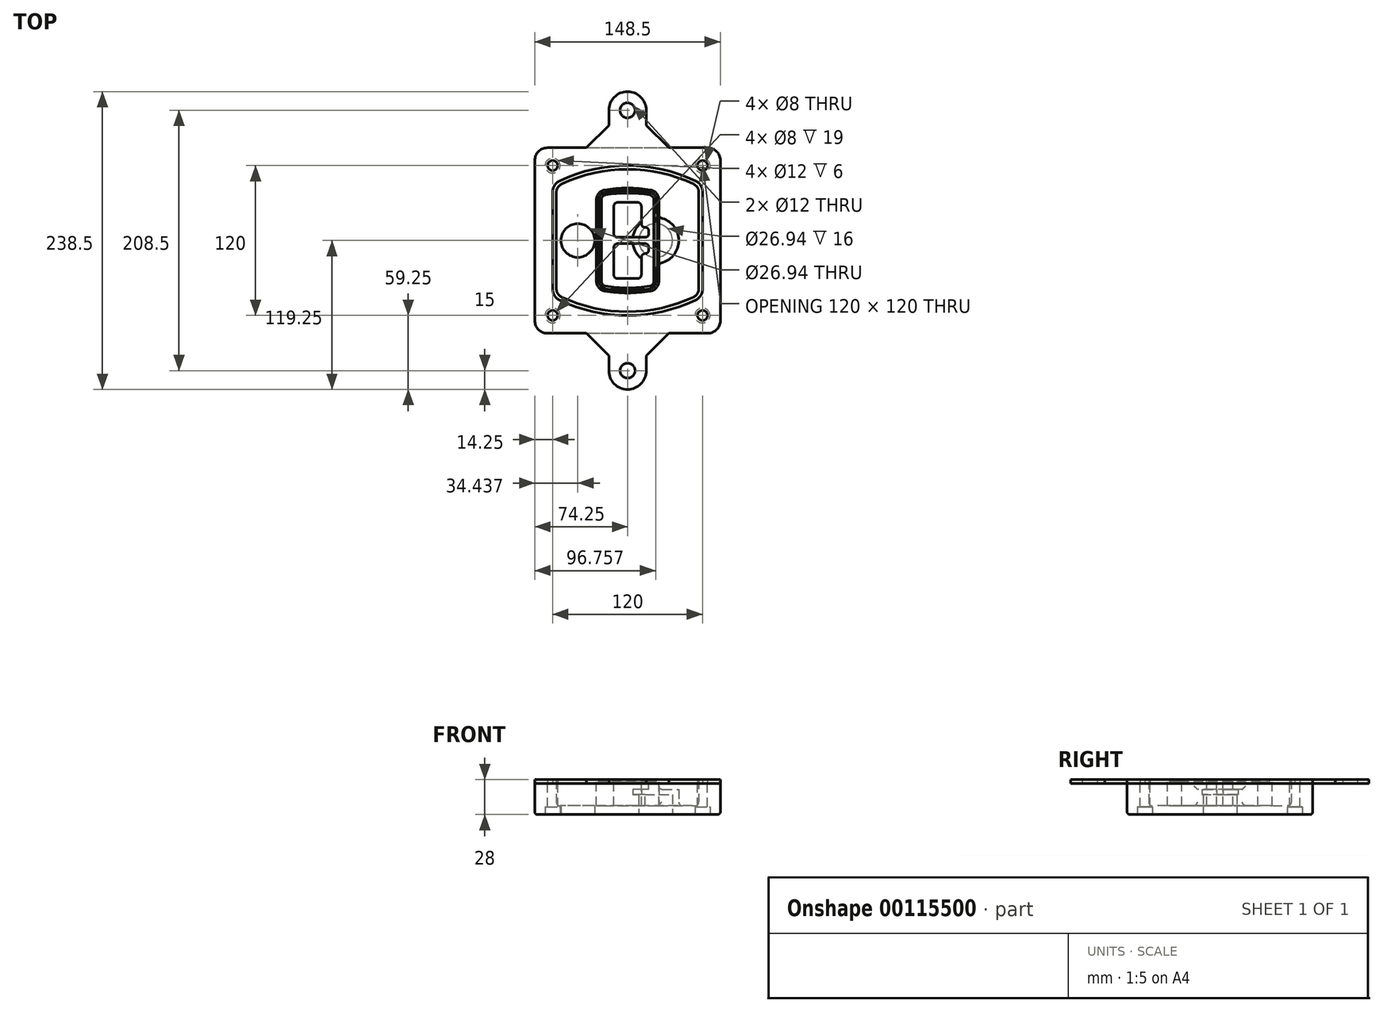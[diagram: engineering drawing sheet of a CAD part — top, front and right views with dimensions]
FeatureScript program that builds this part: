
annotation { "Feature Type Name" : "Feature", "Feature Type Description" : "" }
export const myFeature = defineFeature(function(context is Context, id is Id, definition is map)
    precondition{}
    {
        {
            var Q0;
            Q0=qCreatedBy(makeId("Top.planeOp"),FACE);
            var sketch = newSketch(context, id + "F0", { "sketchPlane" : qUnion([Q0])});
            skPoint(sketch, "E0.rect.middle", {"position": v(0, 0) * mm});
            skLineSegment(sketch, "E1.bottom", {"start": v(-64.25, -74.25) * mm, "end": v(64.25, -74.25) * mm});
            skLineSegment(sketch, "E1.top", {"start": v(-64.25, 74.25) * mm, "end": v(64.25, 74.25) * mm});
            skLineSegment(sketch, "E1.left", {"start": v(-74.25, -64.25) * mm, "end": v(-74.25, 64.25) * mm});
            skLineSegment(sketch, "E1.right", {"start": v(74.25, -64.25) * mm, "end": v(74.25, 64.25) * mm});
            skLineSegment(sketch, "E2", {"start": v(-74.25, 74.25) * mm, "end": v(74.25, -74.25) * mm, "construction": true});
            skLineSegment(sketch, "E3", {"start": v(74.25, 74.25) * mm, "end": v(-74.25, -74.25) * mm, "construction": true});
            skCircle(sketch, "E4", {"center": v(-60, 60) * mm, "radius": 4 * mm});
            skCircle(sketch, "E5", {"center": v(60, 60) * mm, "radius": 4 * mm});
            skCircle(sketch, "E6", {"center": v(60, -60) * mm, "radius": 4 * mm});
            skCircle(sketch, "E7", {"center": v(-60, -60) * mm, "radius": 4 * mm});
            skLineSegment(sketch, "E8", {"start": v(-60, 60) * mm, "end": v(60, 60) * mm, "construction": true});
            skLineSegment(sketch, "E9", {"start": v(60, 60) * mm, "end": v(60, -60) * mm, "construction": true});
            skLineSegment(sketch, "E10", {"start": v(60, -60) * mm, "end": v(-60, -60) * mm, "construction": true});
            skLineSegment(sketch, "E11", {"start": v(-60, -60) * mm, "end": v(-60, 60) * mm, "construction": true});
            skLineSegment(sketch, "E12", {"start": v(-60, 38.83) * mm, "end": v(-60, -38.83) * mm});
            skLineSegment(sketch, "E13", {"start": v(60, 38.83) * mm, "end": v(60, -38.83) * mm});
            skArc(sketch, "E14", {"start": v(54.26, 47.88) * mm, "mid": v(0, 60) * mm, "end": v(-54.26, 47.88) * mm});
            skArc(sketch, "E15", {"start": v(-54.26, -47.88) * mm, "mid": v(0, -60) * mm, "end": v(54.26, -47.88) * mm});
            skLineSegment(sketch, "E16", {"start": v(-60, 0) * mm, "end": v(60, 0) * mm, "construction": true});
            skPoint(sketch, "E17.visualSharp", {"position": v(-60, -45) * mm});
            skArc(sketch, "E17.filletArc", {"start": v(-60, -38.83) * mm, "mid": v(-58.44, -44.2) * mm, "end": v(-54.26, -47.88) * mm});
            skPoint(sketch, "E18.visualSharp", {"position": v(-60, 45) * mm});
            skArc(sketch, "E18.filletArc", {"start": v(-54.26, 47.88) * mm, "mid": v(-58.44, 44.2) * mm, "end": v(-60, 38.83) * mm});
            skPoint(sketch, "E19.visualSharp", {"position": v(60, 45) * mm});
            skArc(sketch, "E19.filletArc", {"start": v(60, 38.83) * mm, "mid": v(58.44, 44.2) * mm, "end": v(54.26, 47.88) * mm});
            skPoint(sketch, "E20.visualSharp", {"position": v(60, -45) * mm});
            skArc(sketch, "E20.filletArc", {"start": v(54.26, -47.88) * mm, "mid": v(58.44, -44.2) * mm, "end": v(60, -38.83) * mm});
            skPoint(sketch, "E21.visualSharp", {"position": v(-74.25, 74.25) * mm});
            skArc(sketch, "E21.filletArc", {"start": v(-64.25, 74.25) * mm, "mid": v(-71.32, 71.32) * mm, "end": v(-74.25, 64.25) * mm});
            skPoint(sketch, "E22.visualSharp", {"position": v(74.25, 74.25) * mm});
            skArc(sketch, "E22.filletArc", {"start": v(74.25, 64.25) * mm, "mid": v(71.32, 71.32) * mm, "end": v(64.25, 74.25) * mm});
            skPoint(sketch, "E23.visualSharp", {"position": v(74.25, -74.25) * mm});
            skArc(sketch, "E23.filletArc", {"start": v(64.25, -74.25) * mm, "mid": v(71.32, -71.32) * mm, "end": v(74.25, -64.25) * mm});
            skPoint(sketch, "E24.visualSharp", {"position": v(-74.25, -74.25) * mm});
            skArc(sketch, "E24.filletArc", {"start": v(-74.25, -64.25) * mm, "mid": v(-71.32, -71.32) * mm, "end": v(-64.25, -74.25) * mm});
            skArc(sketch, "E25.0", {"start": v(57, 38.83) * mm, "mid": v(55.9, 42.58) * mm, "end": v(52.98, 45.17) * mm});
            skLineSegment(sketch, "E25.1", {"start": v(57, 38.83) * mm, "end": v(57, -38.83) * mm});
            skArc(sketch, "E25.2", {"start": v(52.98, -45.17) * mm, "mid": v(55.9, -42.58) * mm, "end": v(57, -38.83) * mm});
            skArc(sketch, "E25.3", {"start": v(-52.98, -45.17) * mm, "mid": v(0, -57) * mm, "end": v(52.98, -45.17) * mm});
            skArc(sketch, "E25.4", {"start": v(-57, -38.83) * mm, "mid": v(-55.9, -42.58) * mm, "end": v(-52.98, -45.17) * mm});
            skArc(sketch, "E25.5", {"start": v(52.98, 45.17) * mm, "mid": v(0, 57) * mm, "end": v(-52.98, 45.17) * mm});
            skLineSegment(sketch, "E25.6", {"start": v(-57, 38.83) * mm, "end": v(-57, -38.83) * mm});
            skArc(sketch, "E25.7", {"start": v(-52.98, 45.17) * mm, "mid": v(-55.9, 42.58) * mm, "end": v(-57, 38.83) * mm});
            skArc(sketch, "E26.0", {"start": v(-55.96, 51.5) * mm, "mid": v(-61.82, 46.33) * mm, "end": v(-64, 38.83) * mm});
            skArc(sketch, "E26.1", {"start": v(55.96, 51.5) * mm, "mid": v(0, 64) * mm, "end": v(-55.96, 51.5) * mm});
            skArc(sketch, "E26.2", {"start": v(64, 38.83) * mm, "mid": v(61.82, 46.33) * mm, "end": v(55.96, 51.5) * mm});
            skLineSegment(sketch, "E26.3", {"start": v(64, 38.83) * mm, "end": v(64, -38.83) * mm});
            skArc(sketch, "E26.4", {"start": v(55.96, -51.5) * mm, "mid": v(61.82, -46.33) * mm, "end": v(64, -38.83) * mm});
            skLineSegment(sketch, "E26.5", {"start": v(-64, 38.83) * mm, "end": v(-64, -38.83) * mm});
            skArc(sketch, "E26.6", {"start": v(-55.96, -51.5) * mm, "mid": v(0, -64) * mm, "end": v(55.96, -51.5) * mm});
            skArc(sketch, "E26.7", {"start": v(-64, -38.83) * mm, "mid": v(-61.82, -46.33) * mm, "end": v(-55.96, -51.5) * mm});
            skSolve(sketch);
        }
        {
            var Q0;
            Q0=makeQuery(id+"F0.imprint","IMPRINT",FACE,{"disambiguationData":[TD([[makeQuery(id+"F0.imprint","IMPRINT",EDGE,{"derivedFrom":sQuery(id+"F0.wireOp",EDGE,"E1.bottom")}),1.0]])]});
            var Q1;
            Q1=makeQuery(id+"F0.imprint","IMPRINT",FACE,{"disambiguationData":[TD([[makeQuery(id+"F0.imprint","IMPRINT",EDGE,{"derivedFrom":sQuery(id+"F0.wireOp",EDGE,"E12")}),1.0]])]});
            var Q2;
            Q2=makeQuery(id+"F0.imprint","IMPRINT",FACE,{"disambiguationData":[TD([[makeQuery(id+"F0.imprint","IMPRINT",EDGE,{"derivedFrom":sQuery(id+"F0.wireOp",EDGE,"E25.0")}),1.0]])]});
            var Q3;
            Q3=makeQuery(id+"F0.imprint","IMPRINT",FACE,{"disambiguationData":[TD([[makeQuery(id+"F0.imprint","IMPRINT",EDGE,{"derivedFrom":sQuery(id+"F0.wireOp",EDGE,"E12")}),-1.0]])]});
            extrude(context, id + "F1", {"entities" : qUnion([Q0, Q1, Q2, Q3]), "oppositeDirection" : true, "depth" : 25 * mm});
        }
        {
            var Q0;
            Q0=makeQuery(id+"F0.imprint","IMPRINT",FACE,{"disambiguationData":[TD([[makeQuery(id+"F0.imprint","IMPRINT",EDGE,{"derivedFrom":sQuery(id+"F0.wireOp",EDGE,"E12")}),1.0]])]});
            extrude(context, id + "F2", {"entities" : qUnion([Q0]), "operationType" : NewBodyOperationType.ADD, "depth" : 3 * mm});
        }
        {
            var Q0;
            Q0=makeQuery(id+"F0.imprint","IMPRINT",FACE,{"disambiguationData":[TD([[makeQuery(id+"F0.imprint","IMPRINT",EDGE,{"derivedFrom":sQuery(id+"F0.wireOp",EDGE,"E25.0")}),1.0]])]});
            extrude(context, id + "F3", {"entities" : qUnion([Q0]), "operationType" : NewBodyOperationType.REMOVE, "oppositeDirection" : true, "depth" : 18 * mm});
        }
        {
            var Q0;
            Q0=makeQuery(id+"F2.opExtrude","CAP_FACE",FACE,{"disambiguationData":[OSD([sQuery(id+"F0.wireOp",EDGE,"E12"),sQuery(id+"F0.wireOp",EDGE,"E13"),sQuery(id+"F0.wireOp",EDGE,"E14"),sQuery(id+"F0.wireOp",EDGE,"E15"),sQuery(id+"F0.wireOp",EDGE,"E17.filletArc"),sQuery(id+"F0.wireOp",EDGE,"E18.filletArc"),sQuery(id+"F0.wireOp",EDGE,"E19.filletArc"),sQuery(id+"F0.wireOp",EDGE,"E20.filletArc"),sQuery(id+"F0.wireOp",EDGE,"E25.0"),sQuery(id+"F0.wireOp",EDGE,"E25.1"),sQuery(id+"F0.wireOp",EDGE,"E25.2"),sQuery(id+"F0.wireOp",EDGE,"E25.3"),sQuery(id+"F0.wireOp",EDGE,"E25.4"),sQuery(id+"F0.wireOp",EDGE,"E25.5"),sQuery(id+"F0.wireOp",EDGE,"E25.6"),sQuery(id+"F0.wireOp",EDGE,"E25.7")])],"isStart":false});
            var sketch = newSketch(context, id + "F4", { "sketchPlane" : qUnion([Q0])});
            skArc(sketch, "E27.0", {"start": v(-18.34, -40.45) * mm, "mid": v(0, -42) * mm, "end": v(18.34, -40.45) * mm});
            skArc(sketch, "E28.0", {"start": v(18.34, 40.45) * mm, "mid": v(0, 42) * mm, "end": v(-18.34, 40.45) * mm});
            skLineSegment(sketch, "E29", {"start": v(-25, 32.57) * mm, "end": v(-25, -32.57) * mm});
            skLineSegment(sketch, "E30", {"start": v(25, 32.57) * mm, "end": v(25, -32.57) * mm});
            skLineSegment(sketch, "E31", {"start": v(-25, 39.1) * mm, "end": v(25, 39.1) * mm, "construction": true});
            skLineSegment(sketch, "E32", {"start": v(-25, -39.1) * mm, "end": v(25, -39.1) * mm, "construction": true});
            skPoint(sketch, "E33.visualSharp", {"position": v(-25, 39.1) * mm});
            skArc(sketch, "E33.filletArc", {"start": v(-18.34, 40.45) * mm, "mid": v(-23.11, 37.73) * mm, "end": v(-25, 32.57) * mm});
            skPoint(sketch, "E34.visualSharp", {"position": v(25, 39.1) * mm});
            skArc(sketch, "E34.filletArc", {"start": v(25, 32.57) * mm, "mid": v(23.11, 37.73) * mm, "end": v(18.34, 40.45) * mm});
            skPoint(sketch, "E35.visualSharp", {"position": v(25, -39.1) * mm});
            skArc(sketch, "E35.filletArc", {"start": v(18.34, -40.45) * mm, "mid": v(23.11, -37.73) * mm, "end": v(25, -32.57) * mm});
            skPoint(sketch, "E36.visualSharp", {"position": v(-25, -39.1) * mm});
            skArc(sketch, "E36.filletArc", {"start": v(-25, -32.57) * mm, "mid": v(-23.11, -37.73) * mm, "end": v(-18.34, -40.45) * mm});
            skArc(sketch, "E37.0", {"start": v(52.98, 45.17) * mm, "mid": v(0, 57) * mm, "end": v(-52.98, 45.17) * mm});
            skArc(sketch, "E37.1", {"start": v(-52.98, 45.17) * mm, "mid": v(-55.9, 42.58) * mm, "end": v(-57, 38.83) * mm});
            skLineSegment(sketch, "E37.2", {"start": v(-57, 38.83) * mm, "end": v(-57, -38.83) * mm});
            skArc(sketch, "E37.3", {"start": v(-57, -38.83) * mm, "mid": v(-55.9, -42.58) * mm, "end": v(-52.98, -45.17) * mm});
            skArc(sketch, "E37.4", {"start": v(-52.98, -45.17) * mm, "mid": v(0, -57) * mm, "end": v(52.98, -45.17) * mm});
            skArc(sketch, "E37.5", {"start": v(52.98, -45.17) * mm, "mid": v(55.9, -42.58) * mm, "end": v(57, -38.83) * mm});
            skLineSegment(sketch, "E37.6", {"start": v(57, 38.83) * mm, "end": v(57, -38.83) * mm});
            skArc(sketch, "E37.7", {"start": v(57, 38.83) * mm, "mid": v(55.9, 42.58) * mm, "end": v(52.98, 45.17) * mm});
            skLineSegment(sketch, "E38.0", {"start": v(23, 32.57) * mm, "end": v(23, -32.57) * mm});
            skArc(sketch, "E38.1", {"start": v(18, -38.48) * mm, "mid": v(21.58, -36.44) * mm, "end": v(23, -32.57) * mm});
            skArc(sketch, "E38.2", {"start": v(-18, -38.48) * mm, "mid": v(0, -40) * mm, "end": v(18, -38.48) * mm});
            skArc(sketch, "E38.3", {"start": v(-23, -32.57) * mm, "mid": v(-21.58, -36.44) * mm, "end": v(-18, -38.48) * mm});
            skLineSegment(sketch, "E38.4", {"start": v(-23, 32.57) * mm, "end": v(-23, -32.57) * mm});
            skArc(sketch, "E38.5", {"start": v(23, 32.57) * mm, "mid": v(21.58, 36.44) * mm, "end": v(18, 38.48) * mm});
            skArc(sketch, "E38.6", {"start": v(-18, 38.48) * mm, "mid": v(-21.58, 36.44) * mm, "end": v(-23, 32.57) * mm});
            skArc(sketch, "E38.7", {"start": v(18, 38.48) * mm, "mid": v(0, 40) * mm, "end": v(-18, 38.48) * mm});
            skArc(sketch, "E39.0", {"start": v(21, 32.57) * mm, "mid": v(20.06, 35.15) * mm, "end": v(17.67, 36.5) * mm});
            skLineSegment(sketch, "E39.1", {"start": v(21, 32.57) * mm, "end": v(21, -32.57) * mm});
            skArc(sketch, "E39.2", {"start": v(17.67, -36.5) * mm, "mid": v(20.06, -35.15) * mm, "end": v(21, -32.57) * mm});
            skArc(sketch, "E39.3", {"start": v(-17.67, -36.5) * mm, "mid": v(0, -38) * mm, "end": v(17.67, -36.5) * mm});
            skArc(sketch, "E39.4", {"start": v(-21, -32.57) * mm, "mid": v(-20.06, -35.15) * mm, "end": v(-17.67, -36.5) * mm});
            skArc(sketch, "E39.5", {"start": v(17.67, 36.5) * mm, "mid": v(0, 38) * mm, "end": v(-17.67, 36.5) * mm});
            skLineSegment(sketch, "E39.6", {"start": v(-21, 32.57) * mm, "end": v(-21, -32.57) * mm});
            skArc(sketch, "E39.7", {"start": v(-17.67, 36.5) * mm, "mid": v(-20.06, 35.15) * mm, "end": v(-21, 32.57) * mm});
            skLineSegment(sketch, "E40", {"start": v(-25, 0) * mm, "end": v(25, 0) * mm, "construction": true});
            skLineSegment(sketch, "E41", {"start": v(-11, 5.5) * mm, "end": v(-11, 27.5) * mm});
            skLineSegment(sketch, "E42", {"start": v(-8, 30.5) * mm, "end": v(8, 30.5) * mm});
            skLineSegment(sketch, "E43", {"start": v(11, 27.5) * mm, "end": v(11, 13.5) * mm});
            skLineSegment(sketch, "E44", {"start": v(14, 10.5) * mm, "end": v(14, 10.5) * mm});
            skLineSegment(sketch, "E45", {"start": v(17, 7.5) * mm, "end": v(17, 5.5) * mm});
            skLineSegment(sketch, "E46", {"start": v(14, 2.5) * mm, "end": v(-8, 2.5) * mm});
            skPoint(sketch, "E47.visualSharp", {"position": v(-11, 30.5) * mm});
            skArc(sketch, "E47.filletArc", {"start": v(-8, 30.5) * mm, "mid": v(-10.12, 29.62) * mm, "end": v(-11, 27.5) * mm});
            skPoint(sketch, "E48.visualSharp", {"position": v(11, 30.5) * mm});
            skArc(sketch, "E48.filletArc", {"start": v(11, 27.5) * mm, "mid": v(10.12, 29.62) * mm, "end": v(8, 30.5) * mm});
            skPoint(sketch, "E49.visualSharp", {"position": v(11, 10.5) * mm});
            skArc(sketch, "E49.filletArc", {"start": v(11, 13.5) * mm, "mid": v(11.88, 11.38) * mm, "end": v(14, 10.5) * mm});
            skPoint(sketch, "E50.visualSharp", {"position": v(17, 10.5) * mm});
            skArc(sketch, "E50.filletArc", {"start": v(17, 7.5) * mm, "mid": v(16.12, 9.62) * mm, "end": v(14, 10.5) * mm});
            skPoint(sketch, "E51.visualSharp", {"position": v(17, 2.5) * mm});
            skArc(sketch, "E51.filletArc", {"start": v(14, 2.5) * mm, "mid": v(16.12, 3.38) * mm, "end": v(17, 5.5) * mm});
            skPoint(sketch, "E52.visualSharp", {"position": v(-11, 2.5) * mm});
            skArc(sketch, "E52.filletArc", {"start": v(-11, 5.5) * mm, "mid": v(-10.12, 3.38) * mm, "end": v(-8, 2.5) * mm});
            skLineSegment(sketch, "E53.0.MirrorCS", {"start": v(14, -2.5) * mm, "end": v(-8, -2.5) * mm});
            skArc(sketch, "E54.0.MirrorCS", {"start": v(-11, -5.5) * mm, "mid": v(-10.12, -3.38) * mm, "end": v(-8, -2.5) * mm});
            skLineSegment(sketch, "E55.0.MirrorCS", {"start": v(-11, -5.5) * mm, "end": v(-11, -27.5) * mm});
            skArc(sketch, "E56.0.MirrorCS", {"start": v(-8, -30.5) * mm, "mid": v(-10.12, -29.62) * mm, "end": v(-11, -27.5) * mm});
            skLineSegment(sketch, "E57.0.MirrorCS", {"start": v(-8, -30.5) * mm, "end": v(8, -30.5) * mm});
            skArc(sketch, "E58.0.MirrorCS", {"start": v(11, -27.5) * mm, "mid": v(10.12, -29.62) * mm, "end": v(8, -30.5) * mm});
            skLineSegment(sketch, "E59.0.MirrorCS", {"start": v(11, -27.5) * mm, "end": v(11, -13.5) * mm});
            skArc(sketch, "E60.0.MirrorCS", {"start": v(11, -13.5) * mm, "mid": v(11.88, -11.38) * mm, "end": v(14, -10.5) * mm});
            skArc(sketch, "E61.0.MirrorCS", {"start": v(17, -7.5) * mm, "mid": v(16.12, -9.62) * mm, "end": v(14, -10.5) * mm});
            skLineSegment(sketch, "E62.0.MirrorCS", {"start": v(17, -7.5) * mm, "end": v(17, -5.5) * mm});
            skArc(sketch, "E63.0.MirrorCS", {"start": v(14, -2.5) * mm, "mid": v(16.12, -3.38) * mm, "end": v(17, -5.5) * mm});
            skSolve(sketch);
        }
        {
            var Q0;
            Q0=makeQuery(id+"F4.imprint","IMPRINT",FACE,{"disambiguationData":[TD([[makeQuery(id+"F4.imprint","IMPRINT",EDGE,{"derivedFrom":sQuery(id+"F4.wireOp",EDGE,"E27.0")}),1.0]])]});
            var Q1;
            Q1=makeQuery(id+"F4.imprint","IMPRINT",FACE,{"disambiguationData":[TD([[makeQuery(id+"F4.imprint","IMPRINT",EDGE,{"derivedFrom":sQuery(id+"F4.wireOp",EDGE,"E38.0")}),-1.0]])]});
            var Q2;
            Q2=makeQuery(id+"F4.imprint","IMPRINT",FACE,{"disambiguationData":[TD([[makeQuery(id+"F4.imprint","IMPRINT",EDGE,{"derivedFrom":sQuery(id+"F4.wireOp",EDGE,"E39.0")}),1.0]])]});
            extrude(context, id + "F5", {"entities" : qUnion([Q0, Q1, Q2]), "operationType" : NewBodyOperationType.ADD, "endBound" : BoundingType.UP_TO_NEXT, "oppositeDirection" : true, "depth" : 25 * mm});
        }
        {
            var Q0;
            Q0=makeQuery(id+"F4.imprint","IMPRINT",FACE,{"disambiguationData":[TD([[makeQuery(id+"F4.imprint","IMPRINT",EDGE,{"derivedFrom":sQuery(id+"F4.wireOp",EDGE,"E38.0")}),-1.0]])]});
            extrude(context, id + "F6", {"entities" : qUnion([Q0]), "operationType" : NewBodyOperationType.REMOVE, "oppositeDirection" : true, "depth" : 2 * mm});
        }
        {
            var Q0;
            Q0=makeQuery(id+"F1.opExtrude","CAP_FACE",FACE,{"disambiguationData":[OSD([sQuery(id+"F0.wireOp",EDGE,"E1.bottom"),sQuery(id+"F0.wireOp",EDGE,"E1.top"),sQuery(id+"F0.wireOp",EDGE,"E1.left"),sQuery(id+"F0.wireOp",EDGE,"E1.right"),sQuery(id+"F0.wireOp",EDGE,"E4"),sQuery(id+"F0.wireOp",EDGE,"E5"),sQuery(id+"F0.wireOp",EDGE,"E6"),sQuery(id+"F0.wireOp",EDGE,"E7"),sQuery(id+"F0.wireOp",EDGE,"E21.filletArc"),sQuery(id+"F0.wireOp",EDGE,"E22.filletArc"),sQuery(id+"F0.wireOp",EDGE,"E23.filletArc"),sQuery(id+"F0.wireOp",EDGE,"E24.filletArc")])],"isStart":false});
            var sketch = newSketch(context, id + "F7", { "sketchPlane" : qUnion([Q0])});
            skCircle(sketch, "E64", {"center": v(22.5, 0) * mm, "radius": 13.47 * mm});
            skCircle(sketch, "E65", {"center": v(-39.81, 0) * mm, "radius": 13.47 * mm});
            skLineSegment(sketch, "E66", {"start": v(74.25, 0) * mm, "end": v(-74.25, 0) * mm});
            skCircle(sketch, "E67", {"center": v(22.5, 0) * mm, "radius": 18.47 * mm});
            skCircle(sketch, "E68", {"center": v(60, -60) * mm, "radius": 6 * mm});
            skCircle(sketch, "E69", {"center": v(-60, -60) * mm, "radius": 6 * mm});
            skCircle(sketch, "E70", {"center": v(-60, 60) * mm, "radius": 6 * mm});
            skCircle(sketch, "E71", {"center": v(60, 60) * mm, "radius": 6 * mm});
            skSolve(sketch);
        }
        {
            var Q0;
            {var subQ1=sQuery(id+"F7.wireOp",EDGE,"E66");var subQ4=sQuery(id+"F7.wireOp",EDGE,"E64");var subQ6=makeQuery(id+"F7.imprint","INTERSECT",VERTEX,{"disambiguationData":[OD(0.0)],"derivedFrom":[subQ4,subQ1]});Q0=makeQuery(id+"F7.imprint","IMPRINT",FACE,{"disambiguationData":[TD([[makeQuery(id+"F7.imprint","IMPRINT",EDGE,{"disambiguationData":[TD([[subQ6,-1.0]])],"derivedFrom":subQ4}),-1.0]])]});}
            var Q1;
            {var subQ0=sQuery(id+"F7.wireOp",EDGE,"E66");var subQ1=sQuery(id+"F7.wireOp",EDGE,"E64");var subQ3=makeQuery(id+"F7.imprint","INTERSECT",VERTEX,{"disambiguationData":[OD(0.0)],"derivedFrom":[subQ1,subQ0]});Q1=makeQuery(id+"F7.imprint","IMPRINT",FACE,{"disambiguationData":[TD([[makeQuery(id+"F7.imprint","IMPRINT",EDGE,{"disambiguationData":[TD([[subQ3,-1.0]])],"derivedFrom":subQ1}),1.0]])]});}
            var Q2;
            {var subQ0=sQuery(id+"F7.wireOp",EDGE,"E66");var subQ1=sQuery(id+"F7.wireOp",EDGE,"E64");var subQ3=makeQuery(id+"F7.imprint","INTERSECT",VERTEX,{"disambiguationData":[OD(0.0)],"derivedFrom":[subQ1,subQ0]});Q2=makeQuery(id+"F7.imprint","IMPRINT",FACE,{"disambiguationData":[TD([[makeQuery(id+"F7.imprint","IMPRINT",EDGE,{"disambiguationData":[TD([[subQ3,1.0]])],"derivedFrom":subQ1}),1.0]])]});}
            var Q3;
            {var subQ1=sQuery(id+"F7.wireOp",EDGE,"E66");var subQ4=sQuery(id+"F7.wireOp",EDGE,"E64");var subQ6=makeQuery(id+"F7.imprint","INTERSECT",VERTEX,{"disambiguationData":[OD(0.0)],"derivedFrom":[subQ4,subQ1]});Q3=makeQuery(id+"F7.imprint","IMPRINT",FACE,{"disambiguationData":[TD([[makeQuery(id+"F7.imprint","IMPRINT",EDGE,{"disambiguationData":[TD([[subQ6,1.0]])],"derivedFrom":subQ4}),-1.0]])]});}
            extrude(context, id + "F8", {"entities" : qUnion([Q0, Q1, Q2, Q3]), "operationType" : NewBodyOperationType.ADD, "oppositeDirection" : true, "depth" : 20 * mm});
        }
        {
            var Q0;
            {var subQ0=sQuery(id+"F7.wireOp",EDGE,"E66");var subQ1=sQuery(id+"F7.wireOp",EDGE,"E64");var subQ3=makeQuery(id+"F7.imprint","INTERSECT",VERTEX,{"disambiguationData":[OD(0.0)],"derivedFrom":[subQ1,subQ0]});Q0=makeQuery(id+"F7.imprint","IMPRINT",FACE,{"disambiguationData":[TD([[makeQuery(id+"F7.imprint","IMPRINT",EDGE,{"disambiguationData":[TD([[subQ3,-1.0]])],"derivedFrom":subQ1}),1.0]])]});}
            var Q1;
            {var subQ0=sQuery(id+"F7.wireOp",EDGE,"E66");var subQ1=sQuery(id+"F7.wireOp",EDGE,"E64");var subQ3=makeQuery(id+"F7.imprint","INTERSECT",VERTEX,{"disambiguationData":[OD(0.0)],"derivedFrom":[subQ1,subQ0]});Q1=makeQuery(id+"F7.imprint","IMPRINT",FACE,{"disambiguationData":[TD([[makeQuery(id+"F7.imprint","IMPRINT",EDGE,{"disambiguationData":[TD([[subQ3,1.0]])],"derivedFrom":subQ1}),1.0]])]});}
            extrude(context, id + "F9", {"entities" : qUnion([Q0, Q1]), "operationType" : NewBodyOperationType.REMOVE, "oppositeDirection" : true, "depth" : 16 * mm});
        }
        {
            var Q0;
            {var subQ0=sQuery(id+"F7.wireOp",EDGE,"E66");var subQ1=sQuery(id+"F7.wireOp",EDGE,"E65");var subQ3=makeQuery(id+"F7.imprint","INTERSECT",VERTEX,{"disambiguationData":[OD(0.0)],"derivedFrom":[subQ1,subQ0]});Q0=makeQuery(id+"F7.imprint","IMPRINT",FACE,{"disambiguationData":[TD([[makeQuery(id+"F7.imprint","IMPRINT",EDGE,{"disambiguationData":[TD([[subQ3,-1.0]])],"derivedFrom":subQ1}),1.0]])]});}
            var Q1;
            {var subQ0=sQuery(id+"F7.wireOp",EDGE,"E66");var subQ1=sQuery(id+"F7.wireOp",EDGE,"E65");var subQ3=makeQuery(id+"F7.imprint","INTERSECT",VERTEX,{"disambiguationData":[OD(0.0)],"derivedFrom":[subQ1,subQ0]});Q1=makeQuery(id+"F7.imprint","IMPRINT",FACE,{"disambiguationData":[TD([[makeQuery(id+"F7.imprint","IMPRINT",EDGE,{"disambiguationData":[TD([[subQ3,1.0]])],"derivedFrom":subQ1}),1.0]])]});}
            extrude(context, id + "F10", {"entities" : qUnion([Q0, Q1]), "operationType" : NewBodyOperationType.REMOVE, "oppositeDirection" : true, "depth" : 25 * mm});
        }
        {
            var Q0;
            Q0=makeQuery(id+"F7.imprint","IMPRINT",FACE,{"disambiguationData":[TD([[makeQuery(id+"F7.imprint","IMPRINT",EDGE,{"derivedFrom":sQuery(id+"F7.wireOp",EDGE,"E68")}),1.0]])]});
            var Q1;
            Q1=makeQuery(id+"F7.imprint","IMPRINT",FACE,{"disambiguationData":[TD([[makeQuery(id+"F7.imprint","IMPRINT",EDGE,{"derivedFrom":makeQuery(id+"F1.opExtrude","CAP_EDGE",EDGE,{"disambiguationData":[OSD([sQuery(id+"F0.wireOp",EDGE,"E5")])],"isStart":false})}),-1.0]])]});
            var Q2;
            Q2=makeQuery(id+"F7.imprint","IMPRINT",FACE,{"disambiguationData":[TD([[makeQuery(id+"F7.imprint","IMPRINT",EDGE,{"derivedFrom":sQuery(id+"F7.wireOp",EDGE,"E69")}),1.0]])]});
            var Q3;
            Q3=makeQuery(id+"F7.imprint","IMPRINT",FACE,{"disambiguationData":[TD([[makeQuery(id+"F7.imprint","IMPRINT",EDGE,{"derivedFrom":makeQuery(id+"F1.opExtrude","CAP_EDGE",EDGE,{"disambiguationData":[OSD([sQuery(id+"F0.wireOp",EDGE,"E4")])],"isStart":false})}),-1.0]])]});
            var Q4;
            Q4=makeQuery(id+"F7.imprint","IMPRINT",FACE,{"disambiguationData":[TD([[makeQuery(id+"F7.imprint","IMPRINT",EDGE,{"derivedFrom":sQuery(id+"F7.wireOp",EDGE,"E70")}),1.0]])]});
            var Q5;
            Q5=makeQuery(id+"F7.imprint","IMPRINT",FACE,{"disambiguationData":[TD([[makeQuery(id+"F7.imprint","IMPRINT",EDGE,{"derivedFrom":makeQuery(id+"F1.opExtrude","CAP_EDGE",EDGE,{"disambiguationData":[OSD([sQuery(id+"F0.wireOp",EDGE,"E7")])],"isStart":false})}),-1.0]])]});
            var Q6;
            Q6=makeQuery(id+"F7.imprint","IMPRINT",FACE,{"disambiguationData":[TD([[makeQuery(id+"F7.imprint","IMPRINT",EDGE,{"derivedFrom":sQuery(id+"F7.wireOp",EDGE,"E71")}),1.0]])]});
            var Q7;
            Q7=makeQuery(id+"F7.imprint","IMPRINT",FACE,{"disambiguationData":[TD([[makeQuery(id+"F7.imprint","IMPRINT",EDGE,{"derivedFrom":makeQuery(id+"F1.opExtrude","CAP_EDGE",EDGE,{"disambiguationData":[OSD([sQuery(id+"F0.wireOp",EDGE,"E6")])],"isStart":false})}),-1.0]])]});
            extrude(context, id + "F11", {"entities" : qUnion([Q0, Q1, Q2, Q3, Q4, Q5, Q6, Q7]), "operationType" : NewBodyOperationType.REMOVE, "oppositeDirection" : true, "depth" : 6 * mm});
        }
        {
            var Q0;
            Q0=makeQuery(id+"F9.boolean.opBoolean","COPY",FACE,{"derivedFrom":makeQuery(id+"F9.opExtrude","CAP_FACE",FACE,{"disambiguationData":[OSD([sQuery(id+"F7.wireOp",EDGE,"E64")])],"isStart":false})});
            var sketch = newSketch(context, id + "F12", { "sketchPlane" : qUnion([Q0])});
            skArc(sketch, "E72.0", {"start": v(11, 14.45) * mm, "mid": v(6.45, 9.13) * mm, "end": v(4.2, 2.5) * mm});
            skArc(sketch, "E72.1", {"start": v(4.2, -2.5) * mm, "mid": v(6.45, -9.13) * mm, "end": v(11, -14.45) * mm});
            skLineSegment(sketch, "E73", {"start": v(4.2, -2.5) * mm, "end": v(14, -2.5) * mm});
            skLineSegment(sketch, "E74.0", {"start": v(14, 2.5) * mm, "end": v(4.2, 2.5) * mm});
            skArc(sketch, "E74.1", {"start": v(14, 2.5) * mm, "mid": v(16.12, 3.38) * mm, "end": v(17, 5.5) * mm});
            skLineSegment(sketch, "E74.2", {"start": v(17, 7.5) * mm, "end": v(17, 5.5) * mm});
            skArc(sketch, "E74.3", {"start": v(17, 7.5) * mm, "mid": v(16.12, 9.62) * mm, "end": v(14, 10.5) * mm});
            skArc(sketch, "E74.4", {"start": v(11, 13.5) * mm, "mid": v(11.88, 11.38) * mm, "end": v(14, 10.5) * mm});
            skLineSegment(sketch, "E74.5", {"start": v(11, 14.45) * mm, "end": v(11, 13.5) * mm});
            skLineSegment(sketch, "E74.7", {"start": v(14, -2.5) * mm, "end": v(4.2, -2.5) * mm});
            skArc(sketch, "E74.8", {"start": v(14, -2.5) * mm, "mid": v(16.12, -3.38) * mm, "end": v(17, -5.5) * mm});
            skLineSegment(sketch, "E74.9", {"start": v(17, -7.5) * mm, "end": v(17, -5.5) * mm});
            skArc(sketch, "E74.10", {"start": v(17, -7.5) * mm, "mid": v(16.12, -9.62) * mm, "end": v(14, -10.5) * mm});
            skArc(sketch, "E74.11", {"start": v(11, -13.5) * mm, "mid": v(11.88, -11.38) * mm, "end": v(14, -10.5) * mm});
            skLineSegment(sketch, "E74.12", {"start": v(11, -14.45) * mm, "end": v(11, -13.5) * mm});
            skPoint(sketch, "E75.orphan", {"position": v(11, -27.5) * mm});
            skPoint(sketch, "E76.orphan", {"position": v(-8, -2.5) * mm});
            skPoint(sketch, "E77.orphan", {"position": v(-8, 2.5) * mm});
            skPoint(sketch, "E78.orphan", {"position": v(11, 27.5) * mm});
            skSolve(sketch);
        }
        {
            var Q0;
            {var subQ7=sQuery(id+"F12.wireOp",EDGE,"E72.0");var subQ14=sQuery(id+"F12.wireOp",EDGE,"E72.1");var subQ16=sQuery(id+"F12.wireOp",EDGE,"E74.1");var subQ18=sQuery(id+"F12.wireOp",EDGE,"E74.8");Q0=qUnion([makeQuery(id+"F12.imprint","IMPRINT",FACE,{"disambiguationData":[TD([[makeQuery(id+"F12.imprint","IMPRINT",EDGE,{"derivedFrom":subQ7}),1.0]])]}),makeQuery(id+"F12.imprint","IMPRINT",FACE,{"disambiguationData":[TD([[makeQuery(id+"F12.imprint","IMPRINT",EDGE,{"derivedFrom":subQ14}),1.0]])]}),makeQuery(id+"F12.imprint","IMPRINT",FACE,{"disambiguationData":[TD([[makeQuery(id+"F12.imprint","IMPRINT",EDGE,{"derivedFrom":subQ16}),1.0]])]}),makeQuery(id+"F12.imprint","IMPRINT",FACE,{"disambiguationData":[TD([[makeQuery(id+"F12.imprint","IMPRINT",EDGE,{"derivedFrom":subQ18}),-1.0]])]})]);}
            var Q1;
            Q1=makeQuery(id+"F5.boolean.opBoolean","SPLIT",FACE,{"disambiguationData":[TD([makeQuery(id+"F5.opExtrude","SWEPT_FACE",FACE,{"disambiguationData":[OSD([sQuery(id+"F4.wireOp",EDGE,"E41")])]})])],"derivedFrom":makeQuery(id+"F3.boolean.opBoolean","COPY",FACE,{"derivedFrom":makeQuery(id+"F3.opExtrude","CAP_FACE",FACE,{"disambiguationData":[OSD([sQuery(id+"F0.wireOp",EDGE,"E25.0"),sQuery(id+"F0.wireOp",EDGE,"E25.1"),sQuery(id+"F0.wireOp",EDGE,"E25.2"),sQuery(id+"F0.wireOp",EDGE,"E25.3"),sQuery(id+"F0.wireOp",EDGE,"E25.4"),sQuery(id+"F0.wireOp",EDGE,"E25.5"),sQuery(id+"F0.wireOp",EDGE,"E25.6"),sQuery(id+"F0.wireOp",EDGE,"E25.7")])],"isStart":false})})});
            extrude(context, id + "F13", {"entities" : qUnion([Q0]), "operationType" : NewBodyOperationType.REMOVE, "endBound" : BoundingType.UP_TO_SURFACE, "endBoundEntityFace" : qUnion([Q1]), "depth" : 25 * mm});
        }
        {
            var Q0;
            Q0=makeQuery(id+"F3.boolean.opBoolean","COPY",EDGE,{"derivedFrom":makeQuery(id+"F3.opExtrude","CAP_EDGE",EDGE,{"disambiguationData":[OSD([sQuery(id+"F0.wireOp",EDGE,"E25.6")])],"isStart":false})});
            var Q1;
            Q1=makeQuery(id+"F8.boolean.opBoolean","INTERSECT",EDGE,{"derivedFrom":[makeQuery(id+"F5.opExtrude","SWEPT_FACE",FACE,{"disambiguationData":[OSD([sQuery(id+"F4.wireOp",EDGE,"E30")])]}),makeQuery(id+"F8.opExtrude","CAP_FACE",FACE,{"disambiguationData":[OSD([sQuery(id+"F7.wireOp",EDGE,"E67")])],"isStart":false})]});
            var Q2;
            Q2=makeQuery(id+"F8.boolean.opBoolean","INTERSECT",EDGE,{"disambiguationData":[OD(1.0)],"derivedFrom":[makeQuery(id+"F5.opExtrude","SWEPT_FACE",FACE,{"disambiguationData":[OSD([sQuery(id+"F4.wireOp",EDGE,"E30")])]}),makeQuery(id+"F8.opExtrude","SWEPT_FACE",FACE,{"disambiguationData":[OSD([sQuery(id+"F7.wireOp",EDGE,"E67")])]})]});
            var Q3;
            {var subQ0=sQuery(id+"F4.wireOp",EDGE,"E30");Q3=makeQuery(id+"F8.boolean.opBoolean","SPLIT",EDGE,{"disambiguationData":[TD([makeQuery(id+"F5.opExtrude","SWEPT_FACE",FACE,{"disambiguationData":[OSD([sQuery(id+"F4.wireOp",EDGE,"E35.filletArc")])]})])],"derivedFrom":makeQuery(id+"F5.opExtrude","CAP_EDGE",EDGE,{"disambiguationData":[OSD([subQ0])],"isStart":false})});}
            var Q4;
            {var subQ0=sQuery(id+"F0.wireOp",EDGE,"E25.7");var subQ1=sQuery(id+"F0.wireOp",EDGE,"E25.1");var subQ2=sQuery(id+"F0.wireOp",EDGE,"E25.6");var subQ3=sQuery(id+"F0.wireOp",EDGE,"E25.5");var subQ4=sQuery(id+"F0.wireOp",EDGE,"E25.4");var subQ5=sQuery(id+"F0.wireOp",EDGE,"E25.0");var subQ6=sQuery(id+"F0.wireOp",EDGE,"E25.2");var subQ7=sQuery(id+"F0.wireOp",EDGE,"E25.3");Q4=makeQuery(id+"F8.boolean.opBoolean","INTERSECT",EDGE,{"derivedFrom":[makeQuery(id+"F5.boolean.opBoolean","SPLIT",FACE,{"disambiguationData":[TD([makeQuery(id+"F2.opExtrude","SWEPT_FACE",FACE,{"disambiguationData":[OSD([subQ5])]})])],"derivedFrom":makeQuery(id+"F3.boolean.opBoolean","COPY",FACE,{"derivedFrom":makeQuery(id+"F3.opExtrude","CAP_FACE",FACE,{"disambiguationData":[OSD([subQ5,subQ1,subQ6,subQ7,subQ4,subQ3,subQ2,subQ0])],"isStart":false})})}),makeQuery(id+"F8.opExtrude","SWEPT_FACE",FACE,{"disambiguationData":[OSD([sQuery(id+"F7.wireOp",EDGE,"E67")])]})]});}
            var Q5;
            Q5=makeQuery(id+"F8.boolean.opBoolean","INTERSECT",EDGE,{"disambiguationData":[OD(0.0)],"derivedFrom":[makeQuery(id+"F5.opExtrude","SWEPT_FACE",FACE,{"disambiguationData":[OSD([sQuery(id+"F4.wireOp",EDGE,"E30")])]}),makeQuery(id+"F8.opExtrude","SWEPT_FACE",FACE,{"disambiguationData":[OSD([sQuery(id+"F7.wireOp",EDGE,"E67")])]})]});
            fillet(context, id + "F14", {"entities" : qUnion([Q0, Q1, Q2, Q3, Q4, Q5]), "radius" : 3 * mm, "tangentPropagation" : true, "allowEdgeOverflow" : false});
        }
        {
            var Q0;
            Q0=makeQuery(id+"F1.opExtrude","CAP_EDGE",EDGE,{"disambiguationData":[OSD([sQuery(id+"F0.wireOp",EDGE,"E1.bottom")])],"isStart":false});
            fillet(context, id + "F15", {"entities" : qUnion([Q0]), "radius" : 2 * mm, "tangentPropagation" : true, "allowEdgeOverflow" : false});
        }
        {
            var Q0;
            {var subQ0=sQuery(id+"F0.wireOp",EDGE,"E22.filletArc");var subQ1=sQuery(id+"F0.wireOp",EDGE,"E7");var subQ2=sQuery(id+"F0.wireOp",EDGE,"E6");var subQ3=sQuery(id+"F0.wireOp",EDGE,"E5");var subQ4=sQuery(id+"F0.wireOp",EDGE,"E4");var subQ5=sQuery(id+"F0.wireOp",EDGE,"E1.bottom");var subQ6=sQuery(id+"F0.wireOp",EDGE,"E21.filletArc");var subQ7=sQuery(id+"F0.wireOp",EDGE,"E1.top");var subQ8=sQuery(id+"F0.wireOp",EDGE,"E1.left");var subQ9=sQuery(id+"F0.wireOp",EDGE,"E1.right");var subQ10=sQuery(id+"F0.wireOp",EDGE,"E23.filletArc");var subQ11=sQuery(id+"F0.wireOp",EDGE,"E24.filletArc");Q0=makeQuery(id+"F2.boolean.opBoolean","SPLIT",FACE,{"disambiguationData":[TD([makeQuery(id+"F1.opExtrude","SWEPT_FACE",FACE,{"disambiguationData":[OSD([subQ5])]})])],"derivedFrom":makeQuery(id+"F1.opExtrude","CAP_FACE",FACE,{"disambiguationData":[OSD([subQ5,subQ7,subQ8,subQ9,subQ4,subQ3,subQ2,subQ1,subQ6,subQ0,subQ10,subQ11])],"isStart":true})});}
            var sketch = newSketch(context, id + "F16", { "sketchPlane" : qUnion([Q0])});
            skLineSegment(sketch, "E79.0", {"start": v(-64.25, 74.25) * mm, "end": v(64.25, 74.25) * mm});
            skArc(sketch, "E80.0", {"start": v(74.25, 64.25) * mm, "mid": v(71.32, 71.32) * mm, "end": v(64.25, 74.25) * mm});
            skLineSegment(sketch, "E81.0", {"start": v(74.25, -64.25) * mm, "end": v(74.25, 64.25) * mm});
            skArc(sketch, "E82.0", {"start": v(64.25, -74.25) * mm, "mid": v(71.32, -71.32) * mm, "end": v(74.25, -64.25) * mm});
            skLineSegment(sketch, "E83.0", {"start": v(-64.25, -74.25) * mm, "end": v(64.25, -74.25) * mm});
            skArc(sketch, "E84.0", {"start": v(-74.25, -64.25) * mm, "mid": v(-71.32, -71.32) * mm, "end": v(-64.25, -74.25) * mm});
            skLineSegment(sketch, "E85.0", {"start": v(-74.25, -64.25) * mm, "end": v(-74.25, 64.25) * mm});
            skArc(sketch, "E86.0", {"start": v(-64.25, 74.25) * mm, "mid": v(-71.32, 71.32) * mm, "end": v(-74.25, 64.25) * mm});
            skCircle(sketch, "E87.0", {"center": v(-60, 60) * mm, "radius": 4 * mm});
            skCircle(sketch, "E88.0", {"center": v(60, 60) * mm, "radius": 4 * mm});
            skCircle(sketch, "E89.0", {"center": v(60, -60) * mm, "radius": 4 * mm});
            skCircle(sketch, "E90.0", {"center": v(-60, -60) * mm, "radius": 4 * mm});
            skLineSegment(sketch, "E91.0", {"start": v(-60, 38.83) * mm, "end": v(-60, -38.83) * mm});
            skArc(sketch, "E92.0", {"start": v(-54.26, 47.88) * mm, "mid": v(-58.44, 44.2) * mm, "end": v(-60, 38.83) * mm});
            skArc(sketch, "E93.0", {"start": v(54.26, 47.88) * mm, "mid": v(0, 60) * mm, "end": v(-54.26, 47.88) * mm});
            skArc(sketch, "E94.0", {"start": v(60, 38.83) * mm, "mid": v(58.44, 44.2) * mm, "end": v(54.26, 47.88) * mm});
            skLineSegment(sketch, "E95.0", {"start": v(60, 38.83) * mm, "end": v(60, -38.83) * mm});
            skArc(sketch, "E96.0", {"start": v(54.26, -47.88) * mm, "mid": v(58.44, -44.2) * mm, "end": v(60, -38.83) * mm});
            skArc(sketch, "E97.0", {"start": v(-54.26, -47.88) * mm, "mid": v(0, -60) * mm, "end": v(54.26, -47.88) * mm});
            skArc(sketch, "E98.0", {"start": v(-60, -38.83) * mm, "mid": v(-58.44, -44.2) * mm, "end": v(-54.26, -47.88) * mm});
            skLineSegment(sketch, "E99", {"start": v(0, 74.25) * mm, "end": v(0, 104.25) * mm, "construction": true});
            skCircle(sketch, "E100", {"center": v(0, 104.25) * mm, "radius": 6 * mm});
            skArc(sketch, "E101", {"start": v(15, 104.25) * mm, "mid": v(0, 119.25) * mm, "end": v(-15, 104.25) * mm});
            skLineSegment(sketch, "E102", {"start": v(-15, 104.25) * mm, "end": v(-15, 92.25) * mm});
            skLineSegment(sketch, "E103", {"start": v(-15, 92.25) * mm, "end": v(-33, 74.25) * mm});
            skLineSegment(sketch, "E104", {"start": v(15, 104.25) * mm, "end": v(15, 92.25) * mm});
            skLineSegment(sketch, "E105", {"start": v(15, 92.25) * mm, "end": v(33, 74.25) * mm});
            skLineSegment(sketch, "E106", {"start": v(-74.25, 0) * mm, "end": v(74.25, 0) * mm, "construction": true});
            skLineSegment(sketch, "E107.MirrorCS", {"start": v(15, -104.25) * mm, "end": v(15, -92.25) * mm});
            skLineSegment(sketch, "E108.MirrorCS", {"start": v(-15, -104.25) * mm, "end": v(-15, -92.25) * mm});
            skLineSegment(sketch, "E109.MirrorCS", {"start": v(15, -92.25) * mm, "end": v(33, -74.25) * mm});
            skCircle(sketch, "E110.MirrorC", {"center": v(0, -104.25) * mm, "radius": 6 * mm});
            skArc(sketch, "E111.MirrorCS", {"start": v(15, -104.25) * mm, "mid": v(0, -119.25) * mm, "end": v(-15, -104.25) * mm});
            skLineSegment(sketch, "E112.MirrorCS", {"start": v(0, -74.25) * mm, "end": v(0, -104.25) * mm, "construction": true});
            skLineSegment(sketch, "E113.MirrorCS", {"start": v(-15, -92.25) * mm, "end": v(-33, -74.25) * mm});
            skSolve(sketch);
        }
        {
            var Q0;
            Q0=makeQuery(id+"F16.imprint","IMPRINT",FACE,{"disambiguationData":[TD([[makeQuery(id+"F16.imprint","IMPRINT",EDGE,{"derivedFrom":sQuery(id+"F16.wireOp",EDGE,"E100")}),-1.0]])]});
            var Q1;
            {var subQ1=sQuery(id+"F16.wireOp",EDGE,"E80.0");Q1=makeQuery(id+"F16.imprint","IMPRINT",FACE,{"disambiguationData":[TD([[makeQuery(id+"F16.imprint","IMPRINT",EDGE,{"derivedFrom":subQ1}),1.0]])]});}
            var Q2;
            Q2=makeQuery(id+"F16.imprint","IMPRINT",FACE,{"disambiguationData":[TD([[makeQuery(id+"F16.imprint","IMPRINT",EDGE,{"derivedFrom":sQuery(id+"F16.wireOp",EDGE,"E107.MirrorCS")}),1.0]])]});
            var Q3;
            Q3=makeQuery(id+"F2.opExtrude","CAP_FACE",FACE,{"disambiguationData":[OSD([sQuery(id+"F0.wireOp",EDGE,"E12"),sQuery(id+"F0.wireOp",EDGE,"E13"),sQuery(id+"F0.wireOp",EDGE,"E14"),sQuery(id+"F0.wireOp",EDGE,"E15"),sQuery(id+"F0.wireOp",EDGE,"E17.filletArc"),sQuery(id+"F0.wireOp",EDGE,"E18.filletArc"),sQuery(id+"F0.wireOp",EDGE,"E19.filletArc"),sQuery(id+"F0.wireOp",EDGE,"E20.filletArc"),sQuery(id+"F0.wireOp",EDGE,"E25.0"),sQuery(id+"F0.wireOp",EDGE,"E25.1"),sQuery(id+"F0.wireOp",EDGE,"E25.2"),sQuery(id+"F0.wireOp",EDGE,"E25.3"),sQuery(id+"F0.wireOp",EDGE,"E25.4"),sQuery(id+"F0.wireOp",EDGE,"E25.5"),sQuery(id+"F0.wireOp",EDGE,"E25.6"),sQuery(id+"F0.wireOp",EDGE,"E25.7")])],"isStart":false});
            extrude(context, id + "F17", {"entities" : qUnion([Q0, Q1, Q2]), "endBound" : BoundingType.UP_TO_SURFACE, "endBoundEntityFace" : qUnion([Q3]), "depth" : 25 * mm});
        }
    });
